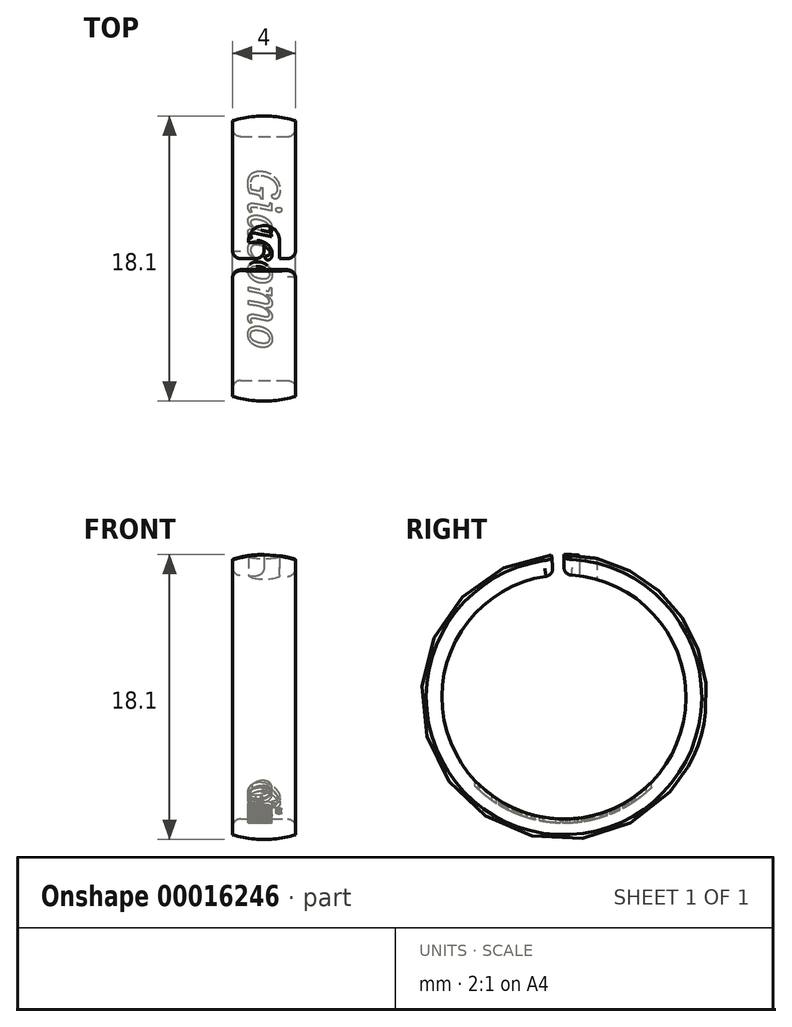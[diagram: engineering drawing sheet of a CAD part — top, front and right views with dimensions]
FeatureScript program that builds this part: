
annotation { "Feature Type Name" : "Feature", "Feature Type Description" : "" }
export const myFeature = defineFeature(function(context is Context, id is Id, definition is map)
    precondition{}
    {
        {
            var Q0;
            Q0=qCreatedBy(makeId("Front.planeOp"),FACE);
            var sketch = newSketch(context, id + "F0", { "sketchPlane" : qUnion([Q0])});
            skLineSegment(sketch, "E0.bottom", {"start": v(-2, 8.75) * mm, "end": v(2, 8.75) * mm});
            skLineSegment(sketch, "E0.top", {"start": v(-1.5, 7.75) * mm, "end": v(1.5, 7.75) * mm});
            skLineSegment(sketch, "E0.left", {"start": v(-2, 8.75) * mm, "end": v(-2, 8.25) * mm});
            skLineSegment(sketch, "E0.right", {"start": v(2, 8.75) * mm, "end": v(2, 8.25) * mm});
            skLineSegment(sketch, "E1", {"start": v(-3.35, 0) * mm, "end": v(5.11, 0) * mm, "construction": true});
            skLineSegment(sketch, "E2", {"start": v(0, 9.74) * mm, "end": v(0, -6.6) * mm, "construction": true});
            skPoint(sketch, "E3.visualSharp", {"position": v(-2, 7.75) * mm});
            skArc(sketch, "E3.filletArc", {"start": v(-2, 8.25) * mm, "mid": v(-1.85, 7.9) * mm, "end": v(-1.5, 7.75) * mm});
            skPoint(sketch, "E4.visualSharp", {"position": v(2, 7.75) * mm});
            skArc(sketch, "E4.filletArc", {"start": v(1.5, 7.75) * mm, "mid": v(1.85, 7.9) * mm, "end": v(2, 8.25) * mm});
            skArc(sketch, "E5", {"start": v(2, 8.75) * mm, "mid": v(0, 9.05) * mm, "end": v(-2, 8.75) * mm});
            skSolve(sketch);
        }
        {
            var Q0;
            Q0=makeQuery(id+"F0.imprint","IMPRINT",FACE,{"disambiguationData":[TD([[makeQuery(id+"F0.imprint","IMPRINT",EDGE,{"derivedFrom":sQuery(id+"F0.wireOp",EDGE,"E0.bottom")}),-1.0]])]});
            var Q1;
            Q1=makeQuery(id+"F0.imprint","IMPRINT",FACE,{"disambiguationData":[TD([[makeQuery(id+"F0.imprint","IMPRINT",EDGE,{"derivedFrom":sQuery(id+"F0.wireOp",EDGE,"E0.bottom")}),1.0]])]});
            var Q2;
            Q2=sQuery(id+"F0.wireOp",EDGE,"E1");
            revolve(context, id + "F1", {"entities" : qUnion([Q0, Q1]), "axis" : qUnion([Q2]), "revolveType" : RevolveType.ONE_DIRECTION, "oppositeDirection" : true, "angle" : 355 * degree});
        }
        {
            var Q0;
            Q0=qCreatedBy(makeId("Top.planeOp"),FACE);
            var sketch = newSketch(context, id + "F2", { "sketchPlane" : qUnion([Q0])});
            skLineSegment(sketch, "E6.0", {"start": v(-2, 0) * mm, "end": v(2, 0) * mm});
            skLineSegment(sketch, "E7", {"start": v(0, 0) * mm, "end": v(0, 1) * mm});
            skLineSegment(sketch, "E8", {"start": v(0, 1) * mm, "end": v(-1, 1) * mm});
            skLineSegment(sketch, "E9", {"start": v(-1, 1) * mm, "end": v(-1, 1.1) * mm});
            skLineSegment(sketch, "E10", {"start": v(1, 0) * mm, "end": v(1, 1.1) * mm});
            skArc(sketch, "E11", {"start": v(1, 1.1) * mm, "mid": v(0, 2.1) * mm, "end": v(-1, 1.1) * mm});
            skSolve(sketch);
        }
        {
            var Q0;
            {var subQ1=sQuery(id+"F2.wireOp",EDGE,"E7");Q0=makeQuery(id+"F2.imprint","IMPRINT",FACE,{"disambiguationData":[TD([[makeQuery(id+"F2.imprint","IMPRINT",EDGE,{"derivedFrom":subQ1}),-1.0]])]});}
            extrude(context, id + "F3", {"entities" : qUnion([Q0]), "operationType" : NewBodyOperationType.REMOVE, "endBound" : BoundingType.THROUGH_ALL, "depth" : 25 * mm});
        }
        {
            var Q0;
            Q0=makeQuery(id+"F1.opRevolve","CAP_EDGE",EDGE,{"disambiguationData":[OSD([sQuery(id+"F0.wireOp",EDGE,"E0.left")])],"isStart":true});
            var Q1;
            Q1=makeQuery(id+"F1.opRevolve","CAP_EDGE",EDGE,{"disambiguationData":[OSD([sQuery(id+"F0.wireOp",EDGE,"E3.filletArc")])],"isStart":true});
            var Q2;
            {var subQ0=sQuery(id+"F0.wireOp",EDGE,"E0.top");var subQ1=sQuery(id+"F0.wireOp",EDGE,"E3.filletArc");Q2=makeQuery(id+"F3.boolean.opBoolean","SPLIT",EDGE,{"disambiguationData":[TD([makeQuery(id+"F1.opRevolve","SWEPT_FACE",FACE,{"disambiguationData":[OSD([subQ1])]})])],"derivedFrom":makeQuery(id+"F1.opRevolve","CAP_EDGE",EDGE,{"disambiguationData":[OSD([subQ0])],"isStart":true})});}
            var Q3;
            {var subQ0=sQuery(id+"F0.wireOp",EDGE,"E0.top");var subQ1=sQuery(id+"F0.wireOp",EDGE,"E4.filletArc");Q3=makeQuery(id+"F3.boolean.opBoolean","SPLIT",EDGE,{"disambiguationData":[TD([makeQuery(id+"F1.opRevolve","SWEPT_FACE",FACE,{"disambiguationData":[OSD([subQ1])]})])],"derivedFrom":makeQuery(id+"F1.opRevolve","CAP_EDGE",EDGE,{"disambiguationData":[OSD([subQ0])],"isStart":true})});}
            var Q4;
            Q4=makeQuery(id+"F1.opRevolve","CAP_EDGE",EDGE,{"disambiguationData":[OSD([sQuery(id+"F0.wireOp",EDGE,"E4.filletArc")])],"isStart":true});
            var Q5;
            Q5=makeQuery(id+"F1.opRevolve","CAP_EDGE",EDGE,{"disambiguationData":[OSD([sQuery(id+"F0.wireOp",EDGE,"E0.right")])],"isStart":true});
            var Q6;
            Q6=makeQuery(id+"F1.opRevolve","CAP_EDGE",EDGE,{"disambiguationData":[OSD([sQuery(id+"F0.wireOp",EDGE,"E0.right")])],"isStart":false});
            var Q7;
            Q7=makeQuery(id+"F1.opRevolve","CAP_EDGE",EDGE,{"disambiguationData":[OSD([sQuery(id+"F0.wireOp",EDGE,"E4.filletArc")])],"isStart":false});
            var Q8;
            Q8=makeQuery(id+"F1.opRevolve","CAP_EDGE",EDGE,{"disambiguationData":[OSD([sQuery(id+"F0.wireOp",EDGE,"E0.top")])],"isStart":false});
            fillet(context, id + "F4", {"entities" : qUnion([Q0, Q1, Q2, Q3, Q4, Q5, Q6, Q7, Q8]), "radius" : .5 * mm, "tangentPropagation" : true, "allowEdgeOverflow" : false});
        }
        {
            var Q0;
            {var subQ0=sQuery(id+"F0.wireOp",EDGE,"E0.top");var subQ1=makeQuery(id+"F3.opExtrude","SWEPT_FACE",FACE,{"disambiguationData":[OSD([sQuery(id+"F2.wireOp",EDGE,"E7")])]});var subQ2=sQuery(id+"F0.wireOp",EDGE,"E3.filletArc");Q0=makeQuery(id+"F4.opFillet","BLEND_EDGE",EDGE,{"blendedFrom":[makeQuery(id+"F3.boolean.opBoolean","SPLIT",EDGE,{"disambiguationData":[TD([makeQuery(id+"F1.opRevolve","SWEPT_FACE",FACE,{"disambiguationData":[OSD([subQ2])]})])],"derivedFrom":makeQuery(id+"F1.opRevolve","CAP_EDGE",EDGE,{"disambiguationData":[OSD([subQ0])],"isStart":true})}),makeQuery(id+"F3.boolean.opBoolean","COPY",FACE,{"derivedFrom":subQ1})],"blendedInto":[makeQuery(id+"F3.boolean.opBoolean","COPY",FACE,{"derivedFrom":subQ1})]});}
            var Q1;
            Q1=makeQuery(id+"F3.boolean.opBoolean","COPY",EDGE,{"derivedFrom":makeQuery(id+"F3.opExtrude","SWEPT_EDGE",EDGE,{"disambiguationData":[OSD([sQuery(id+"F2.wireOp",EDGE,"E6.0"),sQuery(id+"F2.wireOp",EDGE,"E7")])]})});
            var Q2;
            Q2=makeQuery(id+"F3.boolean.opBoolean","INTERSECT",EDGE,{"derivedFrom":[makeQuery(id+"F1.opRevolve","SWEPT_FACE",FACE,{"disambiguationData":[OSD([sQuery(id+"F0.wireOp",EDGE,"E0.top")])]}),makeQuery(id+"F3.opExtrude","SWEPT_FACE",FACE,{"disambiguationData":[OSD([sQuery(id+"F2.wireOp",EDGE,"E7")])]})]});
            fillet(context, id + "F5", {"entities" : qUnion([Q0, Q1, Q2]), "radius" : .5 * mm, "tangentPropagation" : true, "allowEdgeOverflow" : false});
        }
        {
            var Q0;
            Q0=qCreatedBy(makeId("Top.planeOp"),FACE);
            var sketch = newSketch(context, id + "F6", { "sketchPlane" : qUnion([Q0])});
            skText(sketch, "E12", { "text": "Giacomo", "fontName": "NotoSerif-Italic.ttf"});
            const initialGuessF6  = {"E12": [-0.001, 0.0057, 0, -1, 0.002]};
            skSetInitialGuess(sketch, initialGuessF6);
            skSolve(sketch);
        }
        {
            var Q0;
            Q0=qCreatedBy(makeId("Right.planeOp"),FACE);
            var sketch = newSketch(context, id + "F7", { "sketchPlane" : qUnion([Q0])});
            skCircle(sketch, "E13", {"center": v(0, 0) * mm, "radius": 8 * mm});
            skSolve(sketch);
        }
        {
            var Q0;
            Q0=sQuery(id+"F7.wireOp",EDGE,"E13");
            extrude(context, id + "F8", {"bodyType" : ExtendedToolBodyType.SURFACE, "surfaceEntities" : qUnion([Q0]), "depth" : 6 * mm, "symmetric" : true});
        }
        {
            var Q0;
            Q0 = qSketchRegion(id + "F6", true);
            var Q1;
            Q1=makeQuery(id+"F8.opExtrude","SWEPT_FACE",FACE,{"disambiguationData":[OSD([sQuery(id+"F7.wireOp",EDGE,"E13")])]});
            extrude(context, id + "F9", {"entities" : qUnion([Q0]), "operationType" : NewBodyOperationType.REMOVE, "endBound" : BoundingType.UP_TO_SURFACE, "oppositeDirection" : true, "endBoundEntityFace" : qUnion([Q1]), "depth" : 25 * mm});
        }
    });
